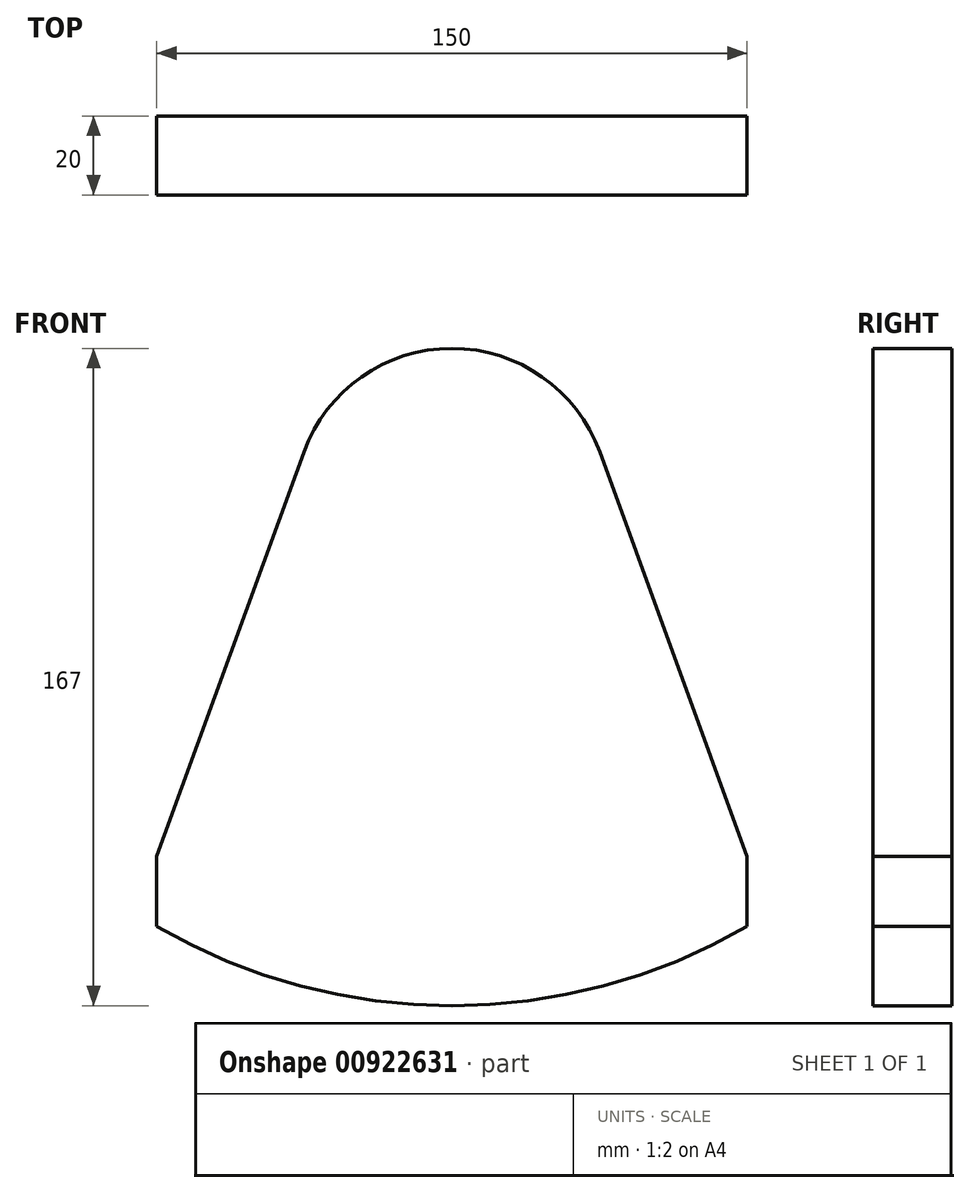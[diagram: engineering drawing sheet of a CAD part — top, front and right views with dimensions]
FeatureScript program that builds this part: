
annotation { "Feature Type Name" : "Feature", "Feature Type Description" : "" }
export const myFeature = defineFeature(function(context is Context, id is Id, definition is map)
    precondition{}
    {
        {
            assignVariable(context, id + "F0", {"name" : "wangen_breite", "anyValue" : 20});
        }
        {
            var Q0;
            Q0=qCreatedBy(makeId("Front.planeOp"),FACE);
            var sketch = newSketch(context, id + "F1", { "sketchPlane" : qUnion([Q0])});
            skLineSegment(sketch, "E0", {"start": v(-37.59, 128.68) * mm, "end": v(-75, 25.9) * mm});
            skLineSegment(sketch, "E1", {"start": v(-75, 25.9) * mm, "end": v(-75, 8.1) * mm});
            skLineSegment(sketch, "E2", {"start": v(75, 8.1) * mm, "end": v(75, 25.9) * mm});
            skLineSegment(sketch, "E3", {"start": v(75, 25.9) * mm, "end": v(37.59, 128.68) * mm});
            skArc(sketch, "E4", {"start": v(37.59, 128.68) * mm, "mid": v(0, 155) * mm, "end": v(-37.59, 128.68) * mm});
            skArc(sketch, "E5", {"start": v(-75, 8.1) * mm, "mid": v(0, -12) * mm, "end": v(75, 8.1) * mm});
            skSolve(sketch);
        }
        {
            var Q0;
            Q0=makeQuery(id+"F1.imprint","IMPRINT",FACE,{"disambiguationData":[TD([[makeQuery(id+"F1.imprint","IMPRINT",EDGE,{"derivedFrom":sQuery(id+"F1.wireOp",EDGE,"E0")}),1.0]])]});
            extrude(context, id + "F2", {"entities" : qUnion([Q0]), "oppositeDirection" : true, "depth" : (getVariable(context, 'wangen_breite')) * mm, "offsetDistance" : 25 * mm});
        }
    });
